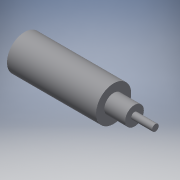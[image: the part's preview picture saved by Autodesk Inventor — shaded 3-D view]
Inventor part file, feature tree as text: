
AUTODESK INVENTOR PART (.ipt)
format: ipt  version: 2016 (Build 200138000, 138)  size: 126,976 bytes
history: native  units: in
note: dims shown in document units (in); Inventor stores cm internally (conversion verified against a paired STEP export)
features: extrude x3, sketch x3
ambient origin geometry x8: Origin, YZ Plane, XZ Plane, XY Plane, X Axis, Y Axis, Z Axis, Center Point
bodies: Solid1 (feature_tree)
feature tree (6):
  extrude  "Extrusion1"  Depth=0.3189in TaperAngle=0.0deg
  extrude  "Extrusion2"  Depth=0.0748in TaperAngle=0.0deg
  extrude  "Extrusion3"  Depth=0.0748in TaperAngle=0.0deg
  sketch  "Sketch1"  dims[d0=0.126in d1=0.3189in d2=0.0in]
  sketch  "Sketch2"  dims[d3=0.0669in d4=0.0748in d5=0.0in]
  sketch  "Sketch3"  dims[d6=0.0236in d7=0.0748in d8=0.0in]
